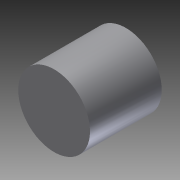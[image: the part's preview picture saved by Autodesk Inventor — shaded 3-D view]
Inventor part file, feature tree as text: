
AUTODESK INVENTOR PART (.ipt)
format: ipt  version: 2012 (Build 160160000, 160)  size: 72,192 bytes
history: native  units: in
note: dims shown in document units (in); Inventor stores cm internally (conversion verified against a paired STEP export)
features: extrude x1, sketch x1
ambient origin geometry x8: Origin, YZ Plane, XZ Plane, XY Plane, X Axis, Y Axis, Z Axis, Center Point
bodies: Solid1 (feature_tree)
feature tree (2):
  extrude  "Extrusion1"  Depth=6.3in TaperAngle=0.0deg
  sketch  "Sketch1"  dims[d0=6.3in d1=6.3in d2=0.0in]
